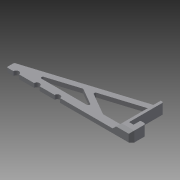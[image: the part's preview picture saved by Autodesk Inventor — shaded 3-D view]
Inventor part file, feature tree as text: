
AUTODESK INVENTOR PART (.ipt)
format: ipt  version: 2014 (Build 180170000, 170)  size: 188,928 bytes
history: native  units: mm
features: chamfer x8, extrude x2, fillet x2, sketch x2, mirror x1
ambient origin geometry x8: Origin, YZ Plane, XZ Plane, XY Plane, X Axis, Y Axis, Z Axis, Center Point
bodies: Solid1 (feature_tree)
feature tree (15):
  extrude  "Extrusion1"  Depth=10.0mm
  extrude  "Extrusion2"  Depth=182.0mm
  chamfer  "Chamfer1"  Distance=11.0mm
  chamfer  "Chamfer2"  Distance=8.0mm
  chamfer  "Chamfer3"  Distance=50.0mm
  chamfer  "Chamfer4"  Distance=30.0mm
  chamfer  "Chamfer5"  Distance=8.0mm
  fillet  "Fillet1"  [1 undecoded]
  fillet  "Fillet2"  Radius=8.0mm
  chamfer  "Chamfer10"  Distance=160.0mm
  chamfer  "Chamfer11"  Distance=30.0mm
  chamfer  "Chamfer12"  Distance=30.0mm
  mirror  "Mirror1"
  sketch  "Sketch1"  dims[d0=8.0mm d1=10.0mm]
  sketch  "Sketch2"  dims[d2=6.5mm d3=182.0mm d4=11.0mm d6=8.0mm d7=50.0mm d8=30.0mm d10=8.0mm d11=30.0deg d12=8.0mm d13=160.0mm d14=30.0mm d15=30.0mm d16=8.0mm d17=8.0mm d18=15.0mm d19=0.0mm d20=70.0mm d21=160.0mm d23=9.0mm d24=0.0mm d25=4.0mm d26=2.0mm d27=45.0deg d28=4.0mm d29=2.0mm d30=45.0deg d31=2.0mm d32=2.0mm d33=45.0deg d34=4.0mm d35=2.0mm d36=45.0deg d37=5.0mm d38=2.0mm d39=45.0deg d52=2.0mm d53=2.0mm d54=1.0mm d55=2.0mm d56=45.0deg d57=1.0mm d58=2.0mm d59=45.0deg d60=1.0mm d61=2.0mm d62=45.0deg]
note: 1 required parameter value undecoded (feature->parameter linkage not recoverable at this tier; creation-order binding heuristic only, values carry confidence <= 0.55)
